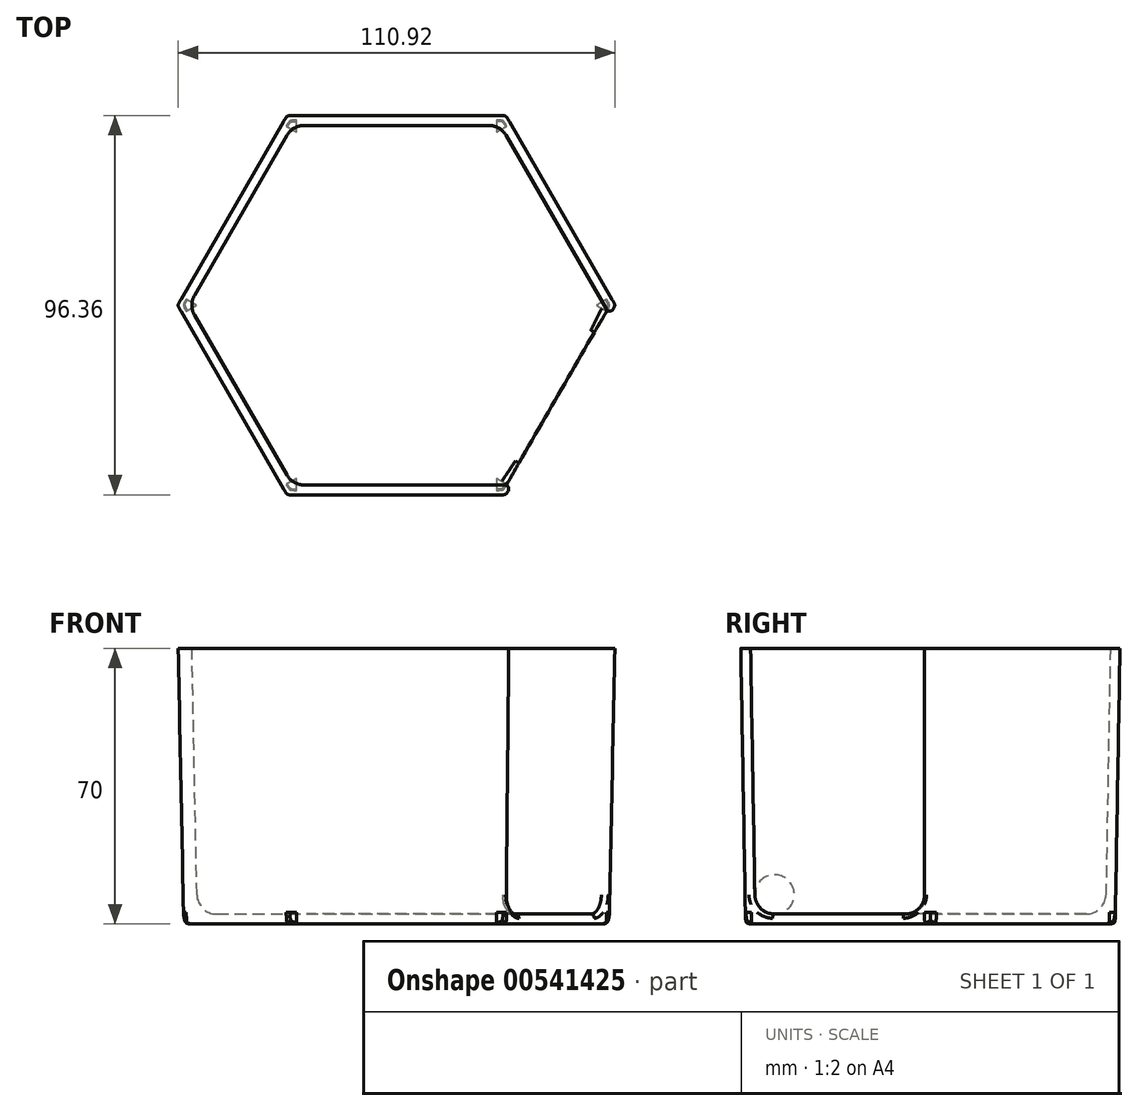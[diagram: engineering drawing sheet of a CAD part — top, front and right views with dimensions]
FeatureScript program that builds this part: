
annotation { "Feature Type Name" : "Feature", "Feature Type Description" : "" }
export const myFeature = defineFeature(function(context is Context, id is Id, definition is map)
    precondition{}
    {
        {
            var Q0;
            Q0=qCreatedBy(makeId("Top.planeOp"),FACE);
            var sketch = newSketch(context, id + "F0", { "sketchPlane" : qUnion([Q0])});
            skCircle(sketch, "E0.cCircle", {"center": v(0, 0) * mm, "radius": 54.22 * mm, "construction": true});
            skLineSegment(sketch, "E0.0", {"start": v(-54.22, 0) * mm, "end": v(-27.11, 46.96) * mm});
            skLineSegment(sketch, "E0.1", {"start": v(-27.11, 46.96) * mm, "end": v(27.11, 46.96) * mm});
            skLineSegment(sketch, "E0.2", {"start": v(27.11, 46.96) * mm, "end": v(54.22, 0) * mm});
            skLineSegment(sketch, "E0.3", {"start": v(54.22, 0) * mm, "end": v(27.11, -46.96) * mm});
            skLineSegment(sketch, "E0.4", {"start": v(27.11, -46.96) * mm, "end": v(-27.11, -46.96) * mm});
            skLineSegment(sketch, "E0.5", {"start": v(-27.11, -46.96) * mm, "end": v(-54.22, 0) * mm});
            skSolve(sketch);
        }
        {
            var Q0;
            Q0=makeQuery(id+"F0.imprint","IMPRINT",FACE,{"disambiguationData":[TD([[makeQuery(id+"F0.imprint","IMPRINT",EDGE,{"derivedFrom":sQuery(id+"F0.wireOp",EDGE,"E0.0")}),-1.0]])]});
            extrude(context, id + "F1", {"entities" : qUnion([Q0]), "depth" : 70 * mm, "offsetDistance" : 25 * mm, "hasDraft" : true, "draftAngle" : 1 * degree});
        }
        {
            var Q0;
            Q0=makeQuery(id+"F1.opExtrude","SWEPT_FACE",FACE,{"disambiguationData":[OSD([sQuery(id+"F0.wireOp",EDGE,"E0.3")])]});
            var sketch = newSketch(context, id + "F2", { "sketchPlane" : qUnion([Q0])});
            skLineSegment(sketch, "E1.bottom", {"start": v(-21.22, 64.95) * mm, "end": v(22.1, 64.95) * mm});
            skLineSegment(sketch, "E1.top", {"start": v(-21.22, 4.97) * mm, "end": v(22.1, 4.97) * mm});
            skLineSegment(sketch, "E1.left", {"start": v(-21.22, 64.95) * mm, "end": v(-21.22, 4.97) * mm});
            skLineSegment(sketch, "E1.right", {"start": v(22.1, 64.95) * mm, "end": v(22.1, 4.97) * mm});
            skSolve(sketch);
        }
        {
            var Q0;
            Q0 = qSketchRegion(id + "F2", true);
            extrude(context, id + "F3", {"entities" : qUnion([Q0]), "operationType" : NewBodyOperationType.REMOVE, "oppositeDirection" : true, "depth" : 25 * mm, "offsetDistance" : 25 * mm});
        }
        {
            var Q0;
            Q0=makeQuery(id+"F3.boolean.opBoolean","COPY",FACE,{"derivedFrom":makeQuery(id+"F3.opExtrude","SWEPT_FACE",FACE,{"disambiguationData":[OSD([sQuery(id+"F2.wireOp",EDGE,"E1.right")])]})});
            var Q1;
            Q1=makeQuery(id+"F3.boolean.opBoolean","COPY",FACE,{"derivedFrom":makeQuery(id+"F3.opExtrude","CAP_FACE",FACE,{"disambiguationData":[OSD([sQuery(id+"F2.wireOp",EDGE,"E1.bottom"),sQuery(id+"F2.wireOp",EDGE,"E1.top"),sQuery(id+"F2.wireOp",EDGE,"E1.left"),sQuery(id+"F2.wireOp",EDGE,"E1.right")])],"isStart":false})});
            var Q2;
            Q2=makeQuery(id+"F3.boolean.opBoolean","COPY",FACE,{"derivedFrom":makeQuery(id+"F3.opExtrude","SWEPT_FACE",FACE,{"disambiguationData":[OSD([sQuery(id+"F2.wireOp",EDGE,"E1.left")])]})});
            var Q3;
            Q3=makeQuery(id+"F1.opExtrude","CAP_FACE",FACE,{"disambiguationData":[OSD([sQuery(id+"F0.wireOp",EDGE,"E0.0"),sQuery(id+"F0.wireOp",EDGE,"E0.1"),sQuery(id+"F0.wireOp",EDGE,"E0.2"),sQuery(id+"F0.wireOp",EDGE,"E0.3"),sQuery(id+"F0.wireOp",EDGE,"E0.4"),sQuery(id+"F0.wireOp",EDGE,"E0.5")])],"isStart":false});
            var Q4;
            Q4=makeQuery(id+"F3.boolean.opBoolean","COPY",FACE,{"derivedFrom":makeQuery(id+"F3.opExtrude","SWEPT_FACE",FACE,{"disambiguationData":[OSD([sQuery(id+"F2.wireOp",EDGE,"E1.bottom")])]})});
            var Q5;
            Q5=makeQuery(id+"F1.opExtrude","SWEPT_FACE",FACE,{"disambiguationData":[OSD([sQuery(id+"F0.wireOp",EDGE,"E0.3")])]});
            var Q6;
            Q6=makeQuery(id+"F3.boolean.opBoolean","COPY",FACE,{"derivedFrom":makeQuery(id+"F3.opExtrude","SWEPT_FACE",FACE,{"disambiguationData":[OSD([sQuery(id+"F2.wireOp",EDGE,"E1.top")])]})});
            shell(context, id + "F4", {"entities" : qUnion([Q0, Q1, Q2, Q3, Q4, Q5, Q6]), "thickness" : 2.5 * mm});
        }
        {
            var Q0;
            Q0=makeQuery(id+"F4.opShell","OFFSET_EDGE",EDGE,{"disambiguationData":[OSD([sQuery(id+"F0.wireOp",EDGE,"E0.4"),sQuery(id+"F0.wireOp",EDGE,"E0.5")])]});
            var Q1;
            Q1=makeQuery(id+"F4.opShell","OFFSET_EDGE",EDGE,{"disambiguationData":[OSD([sQuery(id+"F0.wireOp",EDGE,"E0.0"),sQuery(id+"F0.wireOp",EDGE,"E0.5")])]});
            var Q2;
            Q2=makeQuery(id+"F4.opShell","OFFSET_EDGE",EDGE,{"disambiguationData":[OSD([sQuery(id+"F0.wireOp",EDGE,"E0.0"),sQuery(id+"F0.wireOp",EDGE,"E0.1")])]});
            var Q3;
            Q3=makeQuery(id+"F4.opShell","OFFSET_EDGE",EDGE,{"disambiguationData":[OSD([sQuery(id+"F0.wireOp",EDGE,"E0.1"),sQuery(id+"F0.wireOp",EDGE,"E0.2")])]});
            var Q4;
            {var subQ0=sQuery(id+"F0.wireOp",EDGE,"E0.2");Q4=makeQuery(id+"F4.opShell","OFFSET_EDGE",EDGE,{"disambiguationData":[OSD([subQ0]),TDD([makeQuery(id+"F1.opExtrude","CAP_EDGE",EDGE,{"disambiguationData":[OSD([subQ0])],"isStart":true})])]});}
            var Q5;
            {var subQ0=sQuery(id+"F0.wireOp",EDGE,"E0.1");Q5=makeQuery(id+"F4.opShell","OFFSET_EDGE",EDGE,{"disambiguationData":[OSD([subQ0]),TDD([makeQuery(id+"F1.opExtrude","CAP_EDGE",EDGE,{"disambiguationData":[OSD([subQ0])],"isStart":true})])]});}
            var Q6;
            {var subQ0=sQuery(id+"F0.wireOp",EDGE,"E0.0");Q6=makeQuery(id+"F4.opShell","OFFSET_EDGE",EDGE,{"disambiguationData":[OSD([subQ0]),TDD([makeQuery(id+"F1.opExtrude","CAP_EDGE",EDGE,{"disambiguationData":[OSD([subQ0])],"isStart":true})])]});}
            var Q7;
            {var subQ0=sQuery(id+"F0.wireOp",EDGE,"E0.5");Q7=makeQuery(id+"F4.opShell","OFFSET_EDGE",EDGE,{"disambiguationData":[OSD([subQ0]),TDD([makeQuery(id+"F1.opExtrude","CAP_EDGE",EDGE,{"disambiguationData":[OSD([subQ0])],"isStart":true})])]});}
            var Q8;
            {var subQ0=sQuery(id+"F0.wireOp",EDGE,"E0.4");Q8=makeQuery(id+"F4.opShell","OFFSET_EDGE",EDGE,{"disambiguationData":[OSD([subQ0]),TDD([makeQuery(id+"F1.opExtrude","CAP_EDGE",EDGE,{"disambiguationData":[OSD([subQ0])],"isStart":true})])]});}
            fillet(context, id + "F5", {"entities" : qUnion([Q0, Q1, Q2, Q3, Q4, Q5, Q6, Q7, Q8]), "radius" : 5 * mm, "tangentPropagation" : true, "allowEdgeOverflow" : false});
        }
        {
            var Q0;
            Q0=makeQuery(id+"F1.opExtrude","CAP_FACE",FACE,{"disambiguationData":[OSD([sQuery(id+"F0.wireOp",EDGE,"E0.0"),sQuery(id+"F0.wireOp",EDGE,"E0.1"),sQuery(id+"F0.wireOp",EDGE,"E0.2"),sQuery(id+"F0.wireOp",EDGE,"E0.3"),sQuery(id+"F0.wireOp",EDGE,"E0.4"),sQuery(id+"F0.wireOp",EDGE,"E0.5")])],"isStart":true});
            var Q1;
            Q1=makeQuery(id+"F1.opExtrude","SWEPT_EDGE",EDGE,{"disambiguationData":[OSD([sQuery(id+"F0.wireOp",EDGE,"E0.1"),sQuery(id+"F0.wireOp",EDGE,"E0.2")])]});
            var Q2;
            Q2=makeQuery(id+"F1.opExtrude","SWEPT_EDGE",EDGE,{"disambiguationData":[OSD([sQuery(id+"F0.wireOp",EDGE,"E0.2"),sQuery(id+"F0.wireOp",EDGE,"E0.3")])]});
            var Q3;
            Q3=makeQuery(id+"F1.opExtrude","SWEPT_EDGE",EDGE,{"disambiguationData":[OSD([sQuery(id+"F0.wireOp",EDGE,"E0.3"),sQuery(id+"F0.wireOp",EDGE,"E0.4")])]});
            var Q4;
            Q4=makeQuery(id+"F1.opExtrude","SWEPT_EDGE",EDGE,{"disambiguationData":[OSD([sQuery(id+"F0.wireOp",EDGE,"E0.0"),sQuery(id+"F0.wireOp",EDGE,"E0.1")])]});
            var Q5;
            Q5=makeQuery(id+"F1.opExtrude","SWEPT_EDGE",EDGE,{"disambiguationData":[OSD([sQuery(id+"F0.wireOp",EDGE,"E0.0"),sQuery(id+"F0.wireOp",EDGE,"E0.5")])]});
            var Q6;
            Q6=makeQuery(id+"F1.opExtrude","SWEPT_EDGE",EDGE,{"disambiguationData":[OSD([sQuery(id+"F0.wireOp",EDGE,"E0.4"),sQuery(id+"F0.wireOp",EDGE,"E0.5")])]});
            fillet(context, id + "F6", {"entities" : qUnion([Q0, Q1, Q2, Q3, Q4, Q5, Q6]), "radius" : 3 * mm, "tangentPropagation" : true, "rho" : .8, "crossSection" : FilletCrossSection.CONIC, "allowEdgeOverflow" : false});
        }
        {
            var Q0;
            Q0=makeQuery(id+"F4.opShell","OFFSET_EDGE",EDGE,{"disambiguationData":[OSD([sQuery(id+"F0.wireOp",EDGE,"E0.3"),sQuery(id+"F0.wireOp",EDGE,"E0.4")])]});
            fillet(context, id + "F7", {"entities" : qUnion([Q0]), "radius" : 1 * mm, "tangentPropagation" : true, "allowEdgeOverflow" : false});
        }
    });
